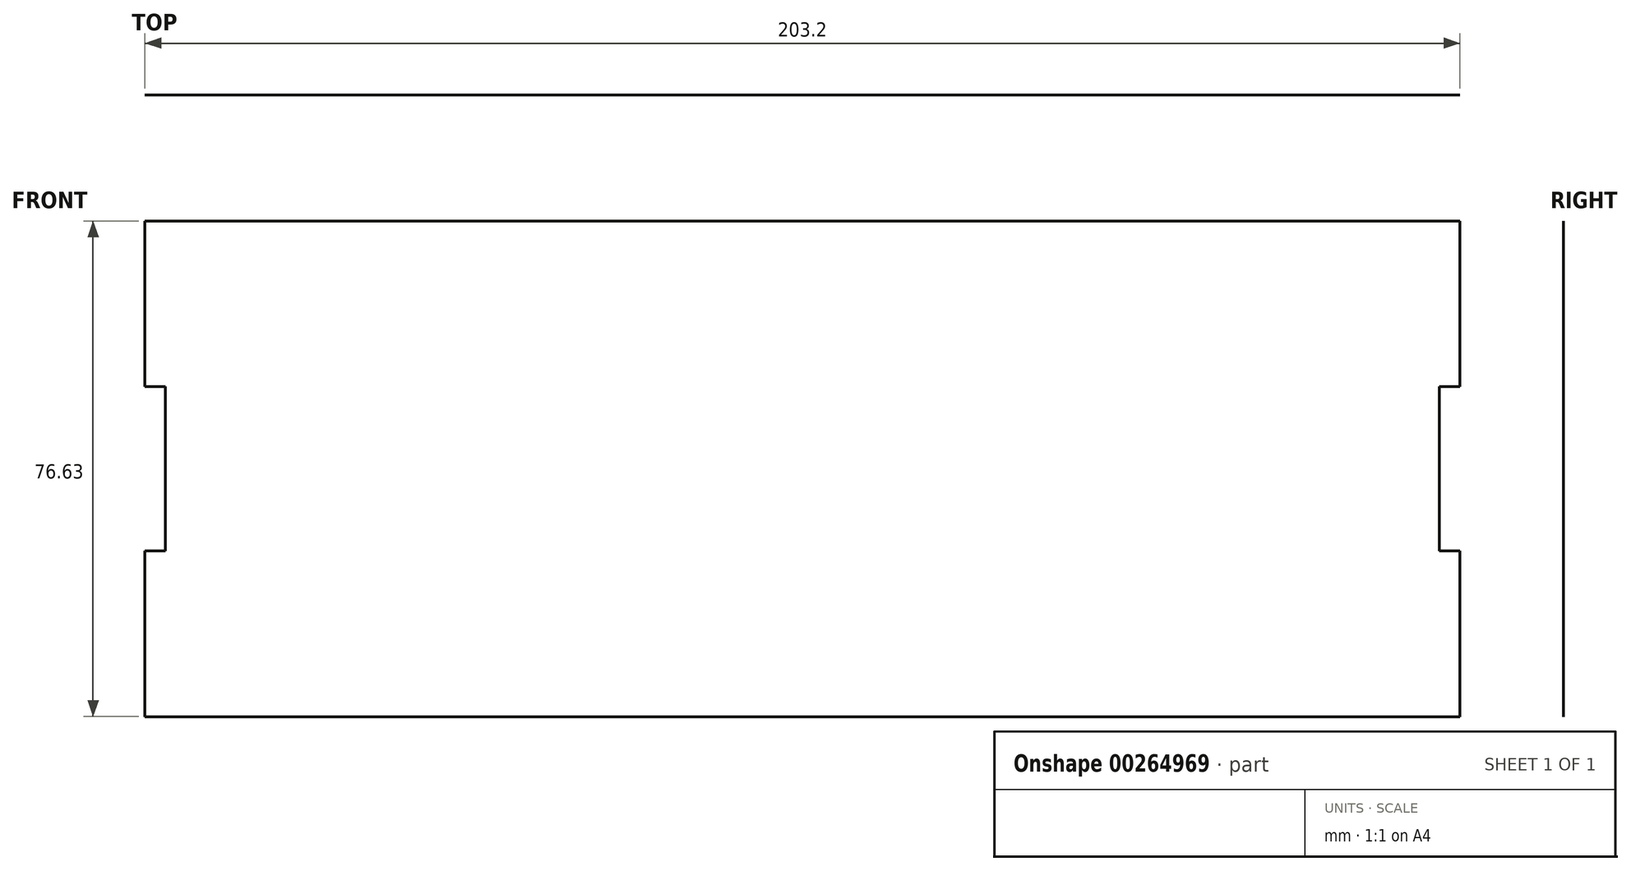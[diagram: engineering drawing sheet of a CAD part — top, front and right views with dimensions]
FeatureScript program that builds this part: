
annotation { "Feature Type Name" : "Feature", "Feature Type Description" : "" }
export const myFeature = defineFeature(function(context is Context, id is Id, definition is map)
    precondition{}
    {
        {
            var Q0;
            Q0=qCreatedBy(makeId("Front.planeOp"),FACE);
            var sketch = newSketch(context, id + "F0", { "sketchPlane" : qUnion([Q0])});
            skLineSegment(sketch, "E0", {"start": v(-101.6, 14.29) * mm, "end": v(-101.6, 39.69) * mm});
            skLineSegment(sketch, "E1", {"start": v(-101.6, -14.29) * mm, "end": v(-101.6, -36.94) * mm});
            skLineSegment(sketch, "E2", {"start": v(-101.6, 39.69) * mm, "end": v(-101.6, 14.29) * mm});
            skLineSegment(sketch, "E3", {"start": v(-101.6, 39.69) * mm, "end": v(0, 39.69) * mm});
            skPoint(sketch, "E4.end.orphan", {"position": v(0, 42.86) * mm});
            skPoint(sketch, "E5.start.orphan", {"position": v(0, 0) * mm});
            skLineSegment(sketch, "E6", {"start": v(-104.78, 14.29) * mm, "end": v(-104.78, 14.16) * mm});
            skLineSegment(sketch, "E7", {"start": v(-101.6, 14.29) * mm, "end": v(-101.6, 14.16) * mm});
            skLineSegment(sketch, "E8", {"start": v(-101.6, -14.29) * mm, "end": v(-101.6, -14.16) * mm});
            skLineSegment(sketch, "E9", {"start": v(-101.6, 14.16) * mm, "end": v(-101.6, 14.07) * mm});
            skPoint(sketch, "E10.end.orphan", {"position": v(-104.78, -14.29) * mm});
            skPoint(sketch, "E10.start.orphan", {"position": v(-104.78, -14.16) * mm});
            skLineSegment(sketch, "E11", {"start": v(-101.6, -36.94) * mm, "end": v(0, -36.94) * mm});
            skPoint(sketch, "E12.end.orphan", {"position": v(0, -42.86) * mm});
            skLineSegment(sketch, "E13.MirrorCS", {"start": v(101.6, 39.69) * mm, "end": v(0, 39.69) * mm});
            skLineSegment(sketch, "E14.MirrorCS", {"start": v(101.6, 14.29) * mm, "end": v(101.6, 39.69) * mm});
            skLineSegment(sketch, "E15.MirrorCS", {"start": v(101.6, 14.29) * mm, "end": v(101.6, 14.16) * mm});
            skLineSegment(sketch, "E16.MirrorCS", {"start": v(101.6, 14.16) * mm, "end": v(101.6, 14.07) * mm});
            skLineSegment(sketch, "E17.MirrorCS", {"start": v(101.6, -14.29) * mm, "end": v(101.6, -14.16) * mm});
            skLineSegment(sketch, "E18.MirrorCS", {"start": v(101.6, -14.29) * mm, "end": v(101.6, -36.94) * mm});
            skLineSegment(sketch, "E19.MirrorCS", {"start": v(101.6, -36.94) * mm, "end": v(0, -36.94) * mm});
            skPoint(sketch, "E20.orphan", {"position": v(0, 39.69) * mm});
            skLineSegment(sketch, "E21", {"start": v(-98.43, 1.37) * mm, "end": v(-98.43, 14.07) * mm});
            skLineSegment(sketch, "E22", {"start": v(-98.43, 14.07) * mm, "end": v(-101.6, 14.07) * mm});
            skLineSegment(sketch, "E23.MirrorCS", {"start": v(-98.43, -11.33) * mm, "end": v(-101.6, -11.33) * mm});
            skLineSegment(sketch, "E24.MirrorCS", {"start": v(-98.43, 1.37) * mm, "end": v(-98.43, -11.33) * mm});
            skLineSegment(sketch, "E25.trimOffspring", {"start": v(-101.6, -11.33) * mm, "end": v(-101.6, -14.16) * mm});
            skPoint(sketch, "E26.start.orphan", {"position": v(-101.6, 1.37) * mm});
            skLineSegment(sketch, "E27.MirrorCS", {"start": v(98.43, 1.37) * mm, "end": v(98.43, 14.07) * mm});
            skLineSegment(sketch, "E28.MirrorCS", {"start": v(98.43, 1.37) * mm, "end": v(98.43, -11.33) * mm});
            skLineSegment(sketch, "E29.MirrorCS", {"start": v(98.43, 14.07) * mm, "end": v(101.6, 14.07) * mm});
            skLineSegment(sketch, "E30.MirrorCS", {"start": v(98.43, -11.33) * mm, "end": v(101.6, -11.33) * mm});
            skLineSegment(sketch, "E31.trimOffspring", {"start": v(101.6, -11.33) * mm, "end": v(101.6, -14.16) * mm});
            skSolve(sketch);
        }
        {
            var Q0;
            Q0=makeQuery(id+"F0.imprint","IMPRINT",FACE,{"disambiguationData":[TD([[makeQuery(id+"F0.imprint","IMPRINT",EDGE,{"derivedFrom":sQuery(id+"F0.wireOp",EDGE,"E1")}),1.0]])]});
            extrude(context, id + "F1", {"entities" : qUnion([Q0]), "depth" : 1 / 203.2 * mm});
        }
    });
